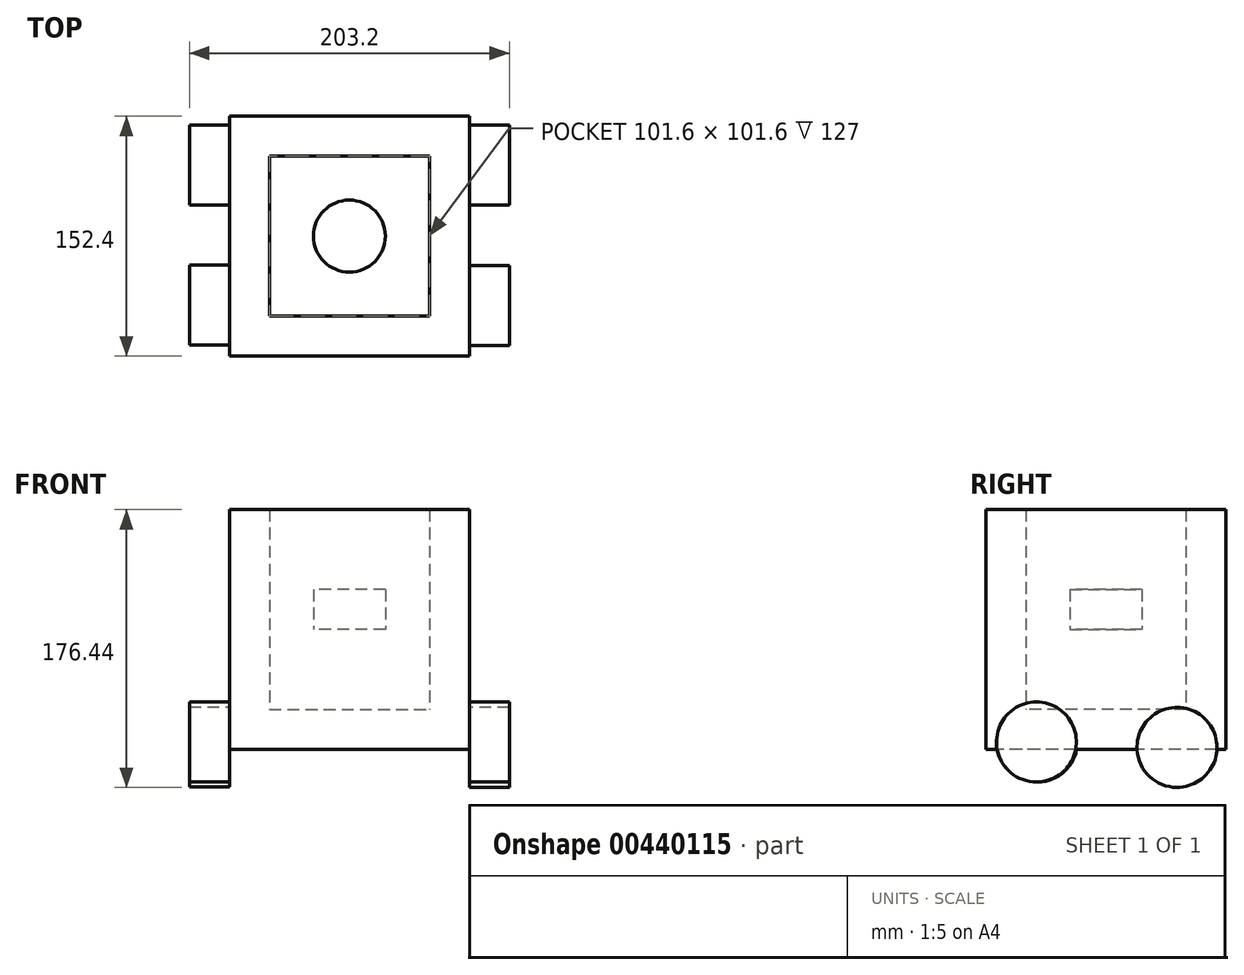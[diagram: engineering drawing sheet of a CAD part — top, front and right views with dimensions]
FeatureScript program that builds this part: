
annotation { "Feature Type Name" : "Feature", "Feature Type Description" : "" }
export const myFeature = defineFeature(function(context is Context, id is Id, definition is map)
    precondition{}
    {
        {
            var Q0;
            Q0=qCreatedBy(makeId("Top.planeOp"),FACE);
            var sketch = newSketch(context, id + "F0", { "sketchPlane" : qUnion([Q0])});
            skLineSegment(sketch, "E0.bottom", {"start": v(-76.2, 76.2) * mm, "end": v(76.2, 76.2) * mm});
            skLineSegment(sketch, "E0.top", {"start": v(-76.2, -76.2) * mm, "end": v(76.2, -76.2) * mm});
            skLineSegment(sketch, "E0.left", {"start": v(-76.2, 76.2) * mm, "end": v(-76.2, -76.2) * mm});
            skLineSegment(sketch, "E0.right", {"start": v(76.2, 76.2) * mm, "end": v(76.2, -76.2) * mm});
            skPoint(sketch, "E0.middle", {"position": v(0, 0) * mm});
            skSolve(sketch);
        }
        {
            var Q0;
            Q0=makeQuery(id+"F0.imprint","IMPRINT",FACE,{"disambiguationData":[TD([[makeQuery(id+"F0.imprint","IMPRINT",EDGE,{"derivedFrom":sQuery(id+"F0.wireOp",EDGE,"E0.bottom")}),-1.0]])]});
            var Q1;
            Q1 = qSketchRegion(id + "F0", true);
            extrude(context, id + "F1", {"entities" : qUnion([Q0, Q1]), "endBound" : BoundingType.SYMMETRIC, "depth" : 152.4 * mm});
        }
        {
            var Q0;
            Q0=makeQuery(id+"F1.opExtrude","SWEPT_FACE",FACE,{"disambiguationData":[OSD([sQuery(id+"F0.wireOp",EDGE,"E0.left")])]});
            var sketch = newSketch(context, id + "F2", { "sketchPlane" : qUnion([Q0])});
            skCircle(sketch, "E1", {"center": v(-45.08, -74.7) * mm, "radius": 25.4 * mm});
            skPoint(sketch, "E1.first.point", {"position": v(-67.5, -62.77) * mm});
            skPoint(sketch, "E1.second.point", {"position": v(-21.82, -64.49) * mm});
            skPoint(sketch, "E1.third.point", {"position": v(-26.39, -91.9) * mm});
            skCircle(sketch, "E2", {"center": v(43.7, -71.47) * mm, "radius": 25.4 * mm});
            skPoint(sketch, "E2.first.point", {"position": v(20.26, -61.67) * mm});
            skPoint(sketch, "E2.second.point", {"position": v(68, -64.09) * mm});
            skPoint(sketch, "E2.third.point", {"position": v(38.93, -46.53) * mm});
            skSolve(sketch);
        }
        {
            var Q0;
            Q0=makeQuery(id+"F1.opExtrude","SWEPT_FACE",FACE,{"disambiguationData":[OSD([sQuery(id+"F0.wireOp",EDGE,"E0.right")])]});
            var sketch = newSketch(context, id + "F3", { "sketchPlane" : qUnion([Q0])});
            skCircle(sketch, "E3", {"center": v(-44.23, -71.44) * mm, "radius": 25.4 * mm});
            skPoint(sketch, "E3.first.point", {"position": v(-68.44, -63.75) * mm});
            skPoint(sketch, "E3.second.point", {"position": v(-20.9, -61.4) * mm});
            skPoint(sketch, "E3.third.point", {"position": v(-38.7, -46.65) * mm});
            skCircle(sketch, "E4", {"center": v(45.05, -74.84) * mm, "radius": 25.4 * mm});
            skPoint(sketch, "E4.first.point", {"position": v(21.85, -64.5) * mm});
            skPoint(sketch, "E4.second.point", {"position": v(67.45, -62.88) * mm});
            skPoint(sketch, "E4.third.point", {"position": v(26.5, -92.2) * mm});
            skSolve(sketch);
        }
        {
            var Q0;
            {var subQ0=sQuery(id+"F3.wireOp",EDGE,"E3");var subQ1=makeQuery(id+"F1.opExtrude","CAP_EDGE",EDGE,{"disambiguationData":[OSD([sQuery(id+"F0.wireOp",EDGE,"E0.right")])],"isStart":true});var subQ2=makeQuery(id+"F3.imprint","INTERSECT",VERTEX,{"disambiguationData":[OD(0.0)],"derivedFrom":[subQ1,subQ0]});Q0=makeQuery(id+"F3.imprint","IMPRINT",FACE,{"disambiguationData":[TD([[makeQuery(id+"F3.imprint","IMPRINT",EDGE,{"disambiguationData":[TD([[subQ2,1.0]])],"derivedFrom":subQ0}),1.0]])]});}
            var Q1;
            {var subQ0=sQuery(id+"F3.wireOp",EDGE,"E4");var subQ1=makeQuery(id+"F1.opExtrude","CAP_EDGE",EDGE,{"disambiguationData":[OSD([sQuery(id+"F0.wireOp",EDGE,"E0.right")])],"isStart":true});var subQ2=makeQuery(id+"F3.imprint","INTERSECT",VERTEX,{"disambiguationData":[OD(0.0)],"derivedFrom":[subQ1,subQ0]});Q1=makeQuery(id+"F3.imprint","IMPRINT",FACE,{"disambiguationData":[TD([[makeQuery(id+"F3.imprint","IMPRINT",EDGE,{"disambiguationData":[TD([[subQ2,-1.0]])],"derivedFrom":subQ0}),1.0]])]});}
            var Q2;
            {var subQ0=sQuery(id+"F3.wireOp",EDGE,"E3");var subQ1=makeQuery(id+"F1.opExtrude","CAP_EDGE",EDGE,{"disambiguationData":[OSD([sQuery(id+"F0.wireOp",EDGE,"E0.right")])],"isStart":true});var subQ2=makeQuery(id+"F3.imprint","INTERSECT",VERTEX,{"disambiguationData":[OD(0.0)],"derivedFrom":[subQ1,subQ0]});Q2=makeQuery(id+"F3.imprint","IMPRINT",FACE,{"disambiguationData":[TD([[makeQuery(id+"F3.imprint","IMPRINT",EDGE,{"disambiguationData":[TD([[subQ2,-1.0]])],"derivedFrom":subQ0}),1.0]])]});}
            var Q3;
            {var subQ0=sQuery(id+"F3.wireOp",EDGE,"E4");var subQ1=makeQuery(id+"F1.opExtrude","CAP_EDGE",EDGE,{"disambiguationData":[OSD([sQuery(id+"F0.wireOp",EDGE,"E0.right")])],"isStart":true});var subQ2=makeQuery(id+"F3.imprint","INTERSECT",VERTEX,{"disambiguationData":[OD(0.0)],"derivedFrom":[subQ1,subQ0]});Q3=makeQuery(id+"F3.imprint","IMPRINT",FACE,{"disambiguationData":[TD([[makeQuery(id+"F3.imprint","IMPRINT",EDGE,{"disambiguationData":[TD([[subQ2,1.0]])],"derivedFrom":subQ0}),1.0]])]});}
            extrude(context, id + "F4", {"entities" : qUnion([Q0, Q1, Q2, Q3]), "operationType" : NewBodyOperationType.ADD, "depth" : 25.4 * mm});
        }
        {
            var Q0;
            {var subQ0=sQuery(id+"F2.wireOp",EDGE,"E1");var subQ1=makeQuery(id+"F1.opExtrude","CAP_EDGE",EDGE,{"disambiguationData":[OSD([sQuery(id+"F0.wireOp",EDGE,"E0.left")])],"isStart":true});var subQ2=makeQuery(id+"F2.imprint","INTERSECT",VERTEX,{"disambiguationData":[OD(0.0)],"derivedFrom":[subQ1,subQ0]});Q0=makeQuery(id+"F2.imprint","IMPRINT",FACE,{"disambiguationData":[TD([[makeQuery(id+"F2.imprint","IMPRINT",EDGE,{"disambiguationData":[TD([[subQ2,1.0]])],"derivedFrom":subQ0}),1.0]])]});}
            var Q1;
            {var subQ0=sQuery(id+"F2.wireOp",EDGE,"E2");var subQ1=makeQuery(id+"F1.opExtrude","CAP_EDGE",EDGE,{"disambiguationData":[OSD([sQuery(id+"F0.wireOp",EDGE,"E0.left")])],"isStart":true});var subQ2=makeQuery(id+"F2.imprint","INTERSECT",VERTEX,{"disambiguationData":[OD(0.0)],"derivedFrom":[subQ1,subQ0]});Q1=makeQuery(id+"F2.imprint","IMPRINT",FACE,{"disambiguationData":[TD([[makeQuery(id+"F2.imprint","IMPRINT",EDGE,{"disambiguationData":[TD([[subQ2,-1.0]])],"derivedFrom":subQ0}),1.0]])]});}
            var Q2;
            {var subQ0=sQuery(id+"F2.wireOp",EDGE,"E1");var subQ1=makeQuery(id+"F1.opExtrude","CAP_EDGE",EDGE,{"disambiguationData":[OSD([sQuery(id+"F0.wireOp",EDGE,"E0.left")])],"isStart":true});var subQ2=makeQuery(id+"F2.imprint","INTERSECT",VERTEX,{"disambiguationData":[OD(0.0)],"derivedFrom":[subQ1,subQ0]});Q2=makeQuery(id+"F2.imprint","IMPRINT",FACE,{"disambiguationData":[TD([[makeQuery(id+"F2.imprint","IMPRINT",EDGE,{"disambiguationData":[TD([[subQ2,-1.0]])],"derivedFrom":subQ0}),1.0]])]});}
            var Q3;
            {var subQ0=sQuery(id+"F2.wireOp",EDGE,"E2");var subQ1=makeQuery(id+"F1.opExtrude","CAP_EDGE",EDGE,{"disambiguationData":[OSD([sQuery(id+"F0.wireOp",EDGE,"E0.left")])],"isStart":true});var subQ2=makeQuery(id+"F2.imprint","INTERSECT",VERTEX,{"disambiguationData":[OD(0.0)],"derivedFrom":[subQ1,subQ0]});Q3=makeQuery(id+"F2.imprint","IMPRINT",FACE,{"disambiguationData":[TD([[makeQuery(id+"F2.imprint","IMPRINT",EDGE,{"disambiguationData":[TD([[subQ2,1.0]])],"derivedFrom":subQ0}),1.0]])]});}
            extrude(context, id + "F5", {"entities" : qUnion([Q0, Q1, Q2, Q3]), "operationType" : NewBodyOperationType.ADD, "depth" : 25.4 * mm});
        }
        {
            var Q0;
            Q0=makeQuery(id+"F1.opExtrude","SWEPT_FACE",FACE,{"disambiguationData":[OSD([sQuery(id+"F0.wireOp",EDGE,"E0.top")])]});
            var sketch = newSketch(context, id + "F6", { "sketchPlane" : qUnion([Q0])});
            skArc(sketch, "E5", {"start": v(-37.37, -57.87) * mm, "mid": v(4.02, -91.5) * mm, "end": v(45.9, -58.47) * mm});
            skSolve(sketch);
        }
        {
            var Q0;
            Q0=sQuery(id+"F6.wireOp",EDGE,"E5");
            extrude(context, id + "F7", {"bodyType" : ToolBodyType.SURFACE, "surfaceEntities" : qUnion([Q0]), "depth" : 25.4 * mm});
        }
        {
            var Q0;
            Q0=makeQuery(id+"F1.opExtrude","CAP_FACE",FACE,{"disambiguationData":[OSD([sQuery(id+"F0.wireOp",EDGE,"E0.bottom"),sQuery(id+"F0.wireOp",EDGE,"E0.top"),sQuery(id+"F0.wireOp",EDGE,"E0.left"),sQuery(id+"F0.wireOp",EDGE,"E0.right")])],"isStart":false});
            shell(context, id + "F8", {"entities" : qUnion([Q0]), "thickness" : 25.4 * mm});
        }
        {
            var Q0;
            Q0=makeQuery(id+"F0.imprint","IMPRINT",FACE,{"disambiguationData":[TD([[makeQuery(id+"F0.imprint","IMPRINT",EDGE,{"derivedFrom":sQuery(id+"F0.wireOp",EDGE,"E0.bottom")}),-1.0]])]});
            var sketch = newSketch(context, id + "F9", { "sketchPlane" : qUnion([Q0])});
            skCircle(sketch, "E6", {"center": v(0, 0) * mm, "radius": 22.86 * mm});
            skSolve(sketch);
        }
        {
            var Q0;
            Q0 = qSketchRegion(id + "F9", true);
            extrude(context, id + "F10", {"entities" : qUnion([Q0]), "depth" : 25.4 * mm});
        }
    });
